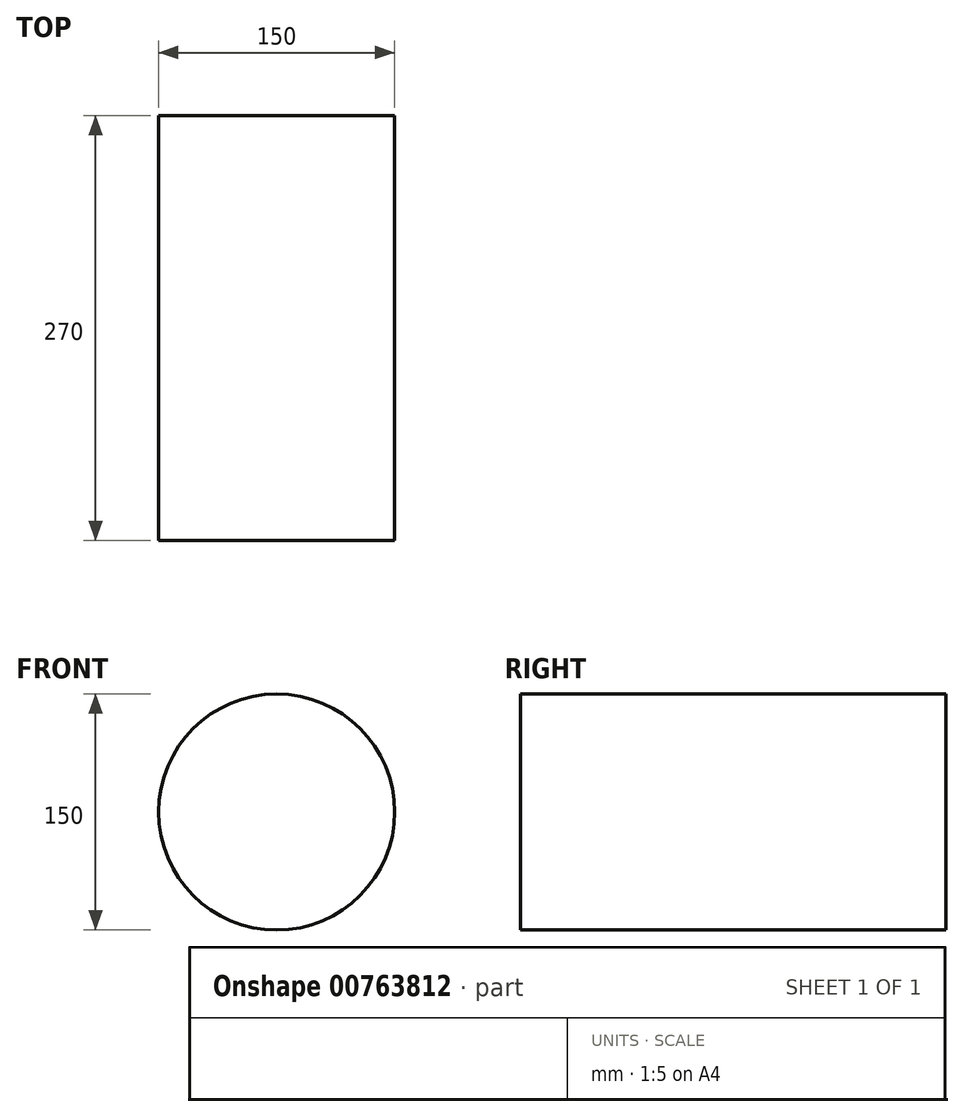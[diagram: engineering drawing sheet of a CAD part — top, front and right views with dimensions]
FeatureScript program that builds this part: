
annotation { "Feature Type Name" : "Feature", "Feature Type Description" : "" }
export const myFeature = defineFeature(function(context is Context, id is Id, definition is map)
    precondition{}
    {
        {
            var Q0;
            Q0=qCreatedBy(makeId("Front.planeOp"),FACE);
            var sketch = newSketch(context, id + "F0", { "sketchPlane" : qUnion([Q0])});
            skCircle(sketch, "E0", {"center": v(0, 0) * mm, "radius": 75 * mm});
            skLineSegment(sketch, "E1", {"start": v(0, 75) * mm, "end": v(0, -75) * mm});
            skSolve(sketch);
        }
        {
            var Q0;
            {var subQ0=sQuery(id+"F0.wireOp",EDGE,"E1");Q0=makeQuery(id+"F0.imprint","IMPRINT",FACE,{"disambiguationData":[TD([[makeQuery(id+"F0.imprint","IMPRINT",EDGE,{"derivedFrom":subQ0}),1.0]])]});}
            var Q1;
            {var subQ0=sQuery(id+"F0.wireOp",EDGE,"E1");Q1=makeQuery(id+"F0.imprint","IMPRINT",FACE,{"disambiguationData":[TD([[makeQuery(id+"F0.imprint","IMPRINT",EDGE,{"derivedFrom":subQ0}),-1.0]])]});}
            extrude(context, id + "F1", {"entities" : qUnion([Q0, Q1]), "oppositeDirection" : true, "depth" : 135 * mm, "offsetDistance" : 25.4 * mm});
        }
        {
            var Q0;
            Q0=makeQuery(id+"F1.opExtrude","CAP_FACE",FACE,{"disambiguationData":[OSD([sQuery(id+"F0.wireOp",EDGE,"E0")])],"isStart":true});
            extrude(context, id + "F2", {"entities" : qUnion([Q0]), "operationType" : NewBodyOperationType.ADD, "depth" : 135 * mm, "offsetDistance" : 25.4 * mm});
        }
        {
            var Q0;
            Q0=qCreatedBy(makeId("Front.planeOp"),FACE);
            var sketch = newSketch(context, id + "F3", { "sketchPlane" : qUnion([Q0])});
            skLineSegment(sketch, "E2", {"start": v(48.27, 76.54) * mm, "end": v(48.27, -75.9) * mm});
            skSolve(sketch);
        }
        {
            var Q0;
            Q0=sQuery(id+"F3.wireOp",EDGE,"E2");
            extrude(context, id + "F4", {"bodyType" : ToolBodyType.SURFACE, "surfaceEntities" : qUnion([Q0]), "depth" : 175.77 * mm, "offsetDistance" : 25.4 * mm});
        }
    });
